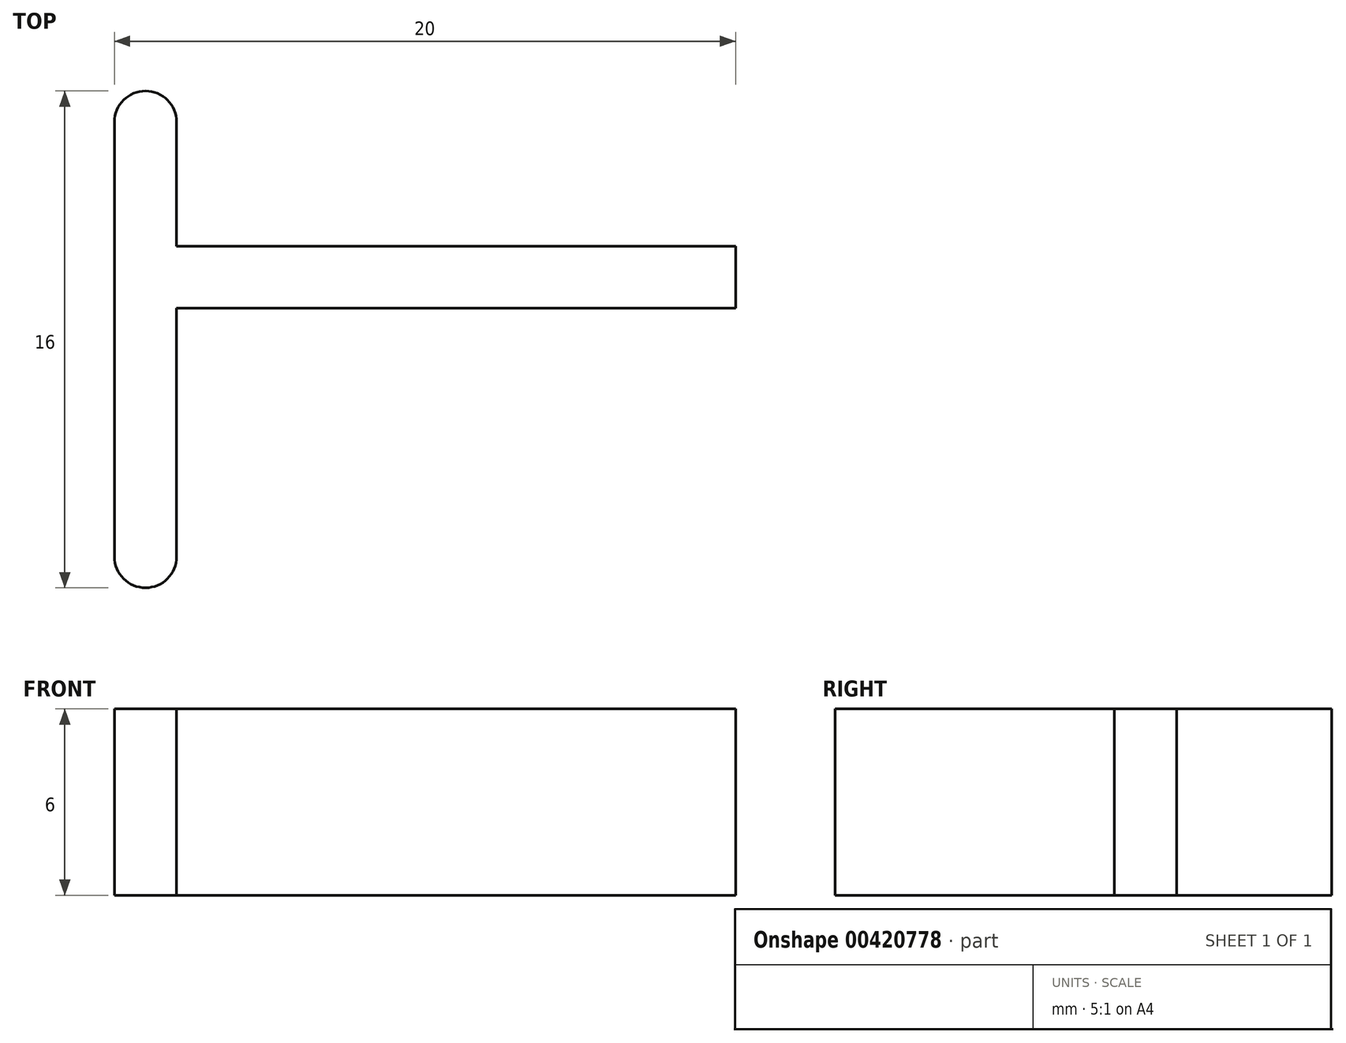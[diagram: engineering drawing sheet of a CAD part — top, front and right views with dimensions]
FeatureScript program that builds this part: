
annotation { "Feature Type Name" : "Feature", "Feature Type Description" : "" }
export const myFeature = defineFeature(function(context is Context, id is Id, definition is map)
    precondition{}
    {
        {
            var Q0;
            Q0=qCreatedBy(makeId("Top.planeOp"),FACE);
            var sketch = newSketch(context, id + "F0", { "sketchPlane" : qUnion([Q0])});
            skLineSegment(sketch, "E0.bottom", {"start": v(0, 5) * mm, "end": v(2, 5) * mm});
            skLineSegment(sketch, "E0.top", {"start": v(0, 0) * mm, "end": v(2, 0) * mm});
            skLineSegment(sketch, "E0.left", {"start": v(0, 5) * mm, "end": v(0, 0) * mm});
            skLineSegment(sketch, "E0.right", {"start": v(2, 5) * mm, "end": v(2, 0) * mm});
            skLineSegment(sketch, "E1.top", {"start": v(0, -11) * mm, "end": v(2, -11) * mm});
            skLineSegment(sketch, "E1.left", {"start": v(0, 0) * mm, "end": v(0, -11) * mm});
            skLineSegment(sketch, "E1.right", {"start": v(2, 0) * mm, "end": v(2, -11) * mm});
            skLineSegment(sketch, "E2.bottom", {"start": v(2, 0) * mm, "end": v(20, 0) * mm});
            skLineSegment(sketch, "E2.top", {"start": v(2, -2) * mm, "end": v(20, -2) * mm});
            skLineSegment(sketch, "E2.left", {"start": v(2, 0) * mm, "end": v(2, -2) * mm});
            skLineSegment(sketch, "E2.right", {"start": v(20, 0) * mm, "end": v(20, -2) * mm});
            skSolve(sketch);
        }
        {
            var Q0;
            Q0=makeQuery(id+"F0.imprint","IMPRINT",FACE,{"disambiguationData":[TD([[makeQuery(id+"F0.imprint","IMPRINT",EDGE,{"derivedFrom":sQuery(id+"F0.wireOp",EDGE,"E0.bottom")}),-1.0]])]});
            var Q1;
            Q1=makeQuery(id+"F0.imprint","IMPRINT",FACE,{"disambiguationData":[TD([[makeQuery(id+"F0.imprint","IMPRINT",EDGE,{"derivedFrom":sQuery(id+"F0.wireOp",EDGE,"E2.bottom")}),-1.0]])]});
            var Q2;
            Q2=makeQuery(id+"F0.imprint","IMPRINT",FACE,{"disambiguationData":[TD([[makeQuery(id+"F0.imprint","IMPRINT",EDGE,{"derivedFrom":sQuery(id+"F0.wireOp",EDGE,"E0.top")}),-1.0]])]});
            extrude(context, id + "F1", {"entities" : qUnion([Q0, Q1, Q2]), "depth" : 6 * mm});
        }
        {
            var Q0;
            Q0=makeQuery(id+"F1.opExtrude","SWEPT_EDGE",EDGE,{"disambiguationData":[OSD([sQuery(id+"F0.wireOp",EDGE,"E0.bottom"),sQuery(id+"F0.wireOp",EDGE,"E0.left")])]});
            var Q1;
            Q1=makeQuery(id+"F1.opExtrude","SWEPT_EDGE",EDGE,{"disambiguationData":[OSD([sQuery(id+"F0.wireOp",EDGE,"E0.bottom"),sQuery(id+"F0.wireOp",EDGE,"E0.right")])]});
            fillet(context, id + "F2", {"entities" : qUnion([Q0, Q1]), "radius" : 1 * mm, "tangentPropagation" : true, "allowEdgeOverflow" : false});
        }
        {
            var Q0;
            Q0=makeQuery(id+"F1.opExtrude","SWEPT_EDGE",EDGE,{"disambiguationData":[OSD([sQuery(id+"F0.wireOp",EDGE,"E1.top"),sQuery(id+"F0.wireOp",EDGE,"E1.left")])]});
            fillet(context, id + "F3", {"entities" : qUnion([Q0]), "radius" : 1 * mm, "tangentPropagation" : true, "allowEdgeOverflow" : false});
        }
        {
            var Q0;
            Q0=makeQuery(id+"F1.opExtrude","SWEPT_EDGE",EDGE,{"disambiguationData":[OSD([sQuery(id+"F0.wireOp",EDGE,"E1.top"),sQuery(id+"F0.wireOp",EDGE,"E1.right")])]});
            fillet(context, id + "F4", {"entities" : qUnion([Q0]), "radius" : 1 * mm, "tangentPropagation" : true, "allowEdgeOverflow" : false});
        }
    });
